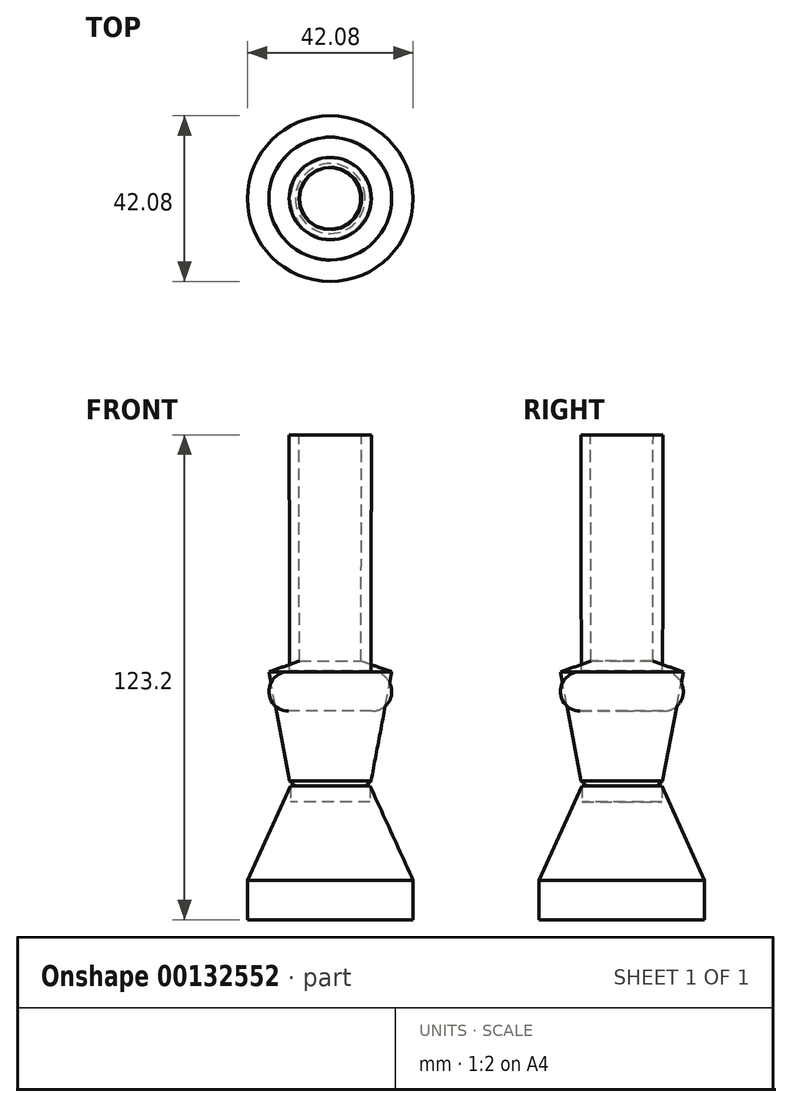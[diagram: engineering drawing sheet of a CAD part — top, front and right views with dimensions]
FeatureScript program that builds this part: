
annotation { "Feature Type Name" : "Feature", "Feature Type Description" : "" }
export const myFeature = defineFeature(function(context is Context, id is Id, definition is map)
    precondition{}
    {
        {
            var Q0;
            Q0=qCreatedBy(makeId("Top.planeOp"),FACE);
            var sketch = newSketch(context, id + "F0", { "sketchPlane" : qUnion([Q0])});
            skCircle(sketch, "E0", {"center": v(0, 0) * mm, "radius": 21.04 * mm});
            skSolve(sketch);
        }
        {
            var Q0;
            Q0=makeQuery(id+"F0.imprint","IMPRINT",FACE,{"disambiguationData":[TD([[makeQuery(id+"F0.imprint","IMPRINT",EDGE,{"derivedFrom":sQuery(id+"F0.wireOp",EDGE,"E0")}),1.0]])]});
            extrude(context, id + "F1", {"entities" : qUnion([Q0]), "depth" : 10 * mm});
        }
        {
            var Q0;
            Q0=makeQuery(id+"F1.opExtrude","CAP_FACE",FACE,{"disambiguationData":[OSD([sQuery(id+"F0.wireOp",EDGE,"E0")])],"isStart":false});
            cPlane(context, id + "F2", {"entities" : qUnion([Q0]), "cplaneType" : CPlaneType.OFFSET, "offset" : 20 * mm, "width" : 150 * mm, "height" : 150 * mm});
        }
        {
            var Q0;
            Q0=qCreatedBy(id+"F2.planeOp",FACE);
            var sketch = newSketch(context, id + "F3", { "sketchPlane" : qUnion([Q0])});
            skCircle(sketch, "E1", {"center": v(0, 0) * mm, "radius": 10.11 * mm});
            skSolve(sketch);
        }
        {
            var Q0;
            Q0=makeQuery(id+"F3.imprint","IMPRINT",FACE,{"disambiguationData":[TD([[makeQuery(id+"F3.imprint","IMPRINT",EDGE,{"derivedFrom":sQuery(id+"F3.wireOp",EDGE,"E1")}),1.0]])]});
            extrude(context, id + "F4", {"entities" : qUnion([Q0]), "depth" : 4 * mm});
        }
        {
            var Q0;
            Q0=makeQuery(id+"F4.opExtrude","CAP_FACE",FACE,{"disambiguationData":[OSD([sQuery(id+"F3.wireOp",EDGE,"E1")])],"isStart":false});
            var Q1;
            Q1=makeQuery(id+"F1.opExtrude","CAP_FACE",FACE,{"disambiguationData":[OSD([sQuery(id+"F0.wireOp",EDGE,"E0")])],"isStart":false});
            loft(context, id + "F5", {"sheetProfilesArray" : [{ "sheetProfileEntities" : qUnion([Q0]) }, { "sheetProfileEntities" : qUnion([Q1]) }]});
        }
        {
            var Q0;
            Q0=qCreatedBy(makeId("Top.planeOp"),FACE);
            cPlane(context, id + "F6", {"entities" : qUnion([Q0]), "cplaneType" : CPlaneType.OFFSET, "offset" : 53 * mm, "width" : 150 * mm, "height" : 150 * mm});
        }
        {
            var Q0;
            Q0=qCreatedBy(id+"F6.planeOp",FACE);
            var sketch = newSketch(context, id + "F7", { "sketchPlane" : qUnion([Q0])});
            skCircle(sketch, "E2", {"center": v(0, 0) * mm, "radius": 15.6 * mm});
            skSolve(sketch);
        }
        {
            var Q0;
            Q0 = qSketchRegion(id + "F7", true);
            extrude(context, id + "F8", {"entities" : qUnion([Q0]), "depth" : 10 * mm});
        }
        {
            var Q0;
            Q0=makeQuery(id+"F8.opExtrude","CAP_FACE",FACE,{"disambiguationData":[OSD([sQuery(id+"F7.wireOp",EDGE,"E2")])],"isStart":false});
            var Q1;
            Q1=makeQuery(id+"F4.opExtrude","CAP_FACE",FACE,{"disambiguationData":[OSD([sQuery(id+"F3.wireOp",EDGE,"E1")])],"isStart":false});
            loft(context, id + "F9", {"sheetProfilesArray" : [{ "sheetProfileEntities" : qUnion([Q0]) }, { "sheetProfileEntities" : qUnion([Q1]) }]});
        }
        {
            var Q0;
            Q0=makeQuery(id+"F8.opExtrude","SWEPT_FACE",FACE,{"disambiguationData":[OSD([sQuery(id+"F7.wireOp",EDGE,"E2")])]});
            fillet(context, id + "F10", {"entities" : qUnion([Q0]), "radius" : 5 * mm, "tangentPropagation" : true, "allowEdgeOverflow" : false});
        }
        {
            var Q0;
            Q0=makeQuery(id+"F9.opLoft","MID_CAP_EDGE",EDGE,{"disambiguationData":[OSD([sQuery(id+"F3.wireOp",EDGE,"E1"),sQuery(id+"F7.wireOp",EDGE,"E2")])],"capPos":1.0});
            chamfer(context, id + "F11", {"entities" : qUnion([Q0]), "width" : 1.5 * mm, "tangentPropagation" : true});
        }
        {
            var Q0;
            Q0=qCreatedBy(makeId("Top.planeOp"),FACE);
            cPlane(context, id + "F12", {"entities" : qUnion([Q0]), "cplaneType" : CPlaneType.OFFSET, "offset" : 63.2 * mm, "width" : 150 * mm, "height" : 150 * mm});
        }
        {
            var Q0;
            Q0=qCreatedBy(id+"F12.planeOp",FACE);
            var sketch = newSketch(context, id + "F13", { "sketchPlane" : qUnion([Q0])});
            skCircle(sketch, "E3", {"center": v(-0.04, 0.02) * mm, "radius": 10.32 * mm});
            skSolve(sketch);
        }
        {
            var Q0;
            Q0=qCreatedBy(id+"F12.planeOp",FACE);
            cPlane(context, id + "F14", {"entities" : qUnion([Q0]), "cplaneType" : CPlaneType.OFFSET, "offset" : 60 * mm, "width" : 150 * mm, "height" : 150 * mm});
        }
        {
            var Q0;
            Q0=qCreatedBy(id+"F14.planeOp",FACE);
            var sketch = newSketch(context, id + "F15", { "sketchPlane" : qUnion([Q0])});
            skCircle(sketch, "E4", {"center": v(0, 0) * mm, "radius": 10.45 * mm});
            skSolve(sketch);
        }
        {
            var Q0;
            Q0=makeQuery(id+"F15.imprint","IMPRINT",FACE,{"disambiguationData":[TD([[makeQuery(id+"F15.imprint","IMPRINT",EDGE,{"derivedFrom":sQuery(id+"F15.wireOp",EDGE,"E4")}),1.0]])]});
            var Q1;
            Q1=makeQuery(id+"F13.imprint","IMPRINT",FACE,{"disambiguationData":[TD([[makeQuery(id+"F13.imprint","IMPRINT",EDGE,{"derivedFrom":sQuery(id+"F13.wireOp",EDGE,"E3")}),1.0]])]});
            loft(context, id + "F16", {"sheetProfilesArray" : [{ "sheetProfileEntities" : qUnion([Q0]) }, { "sheetProfileEntities" : qUnion([Q1]) }]});
        }
        {
            var Q0;
            Q0=makeQuery(id+"F16.opLoft","CAP_FACE",FACE,{"disambiguationData":[OSD([makeQuery(id+"F15.imprint","IMPRINT",FACE,{"disambiguationData":[TD([[makeQuery(id+"F15.imprint","IMPRINT",EDGE,{"derivedFrom":sQuery(id+"F15.wireOp",EDGE,"E4")}),1.0]])]})])],"isStart":true});
            shell(context, id + "F17", {"entities" : qUnion([Q0]), "thickness" : 2.5 * mm});
        }
        {
            var Q0;
            Q0=makeQuery(id+"F17.opShell","OFFSET_FACE",FACE,{"disambiguationData":[OSD([makeQuery(id+"F13.imprint","IMPRINT",FACE,{"disambiguationData":[TD([[makeQuery(id+"F13.imprint","IMPRINT",EDGE,{"derivedFrom":sQuery(id+"F13.wireOp",EDGE,"E3")}),1.0]])]})])]});
            var Q1;
            Q1=makeQuery(id+"F9.opLoft","CAP_FACE",FACE,{"disambiguationData":[OSD([sQuery(id+"F7.wireOp",EDGE,"E2")])],"isStart":true});
            loft(context, id + "F18", {"sheetProfilesArray" : [{ "sheetProfileEntities" : qUnion([Q0]) }, { "sheetProfileEntities" : qUnion([Q1]) }]});
        }
    });
